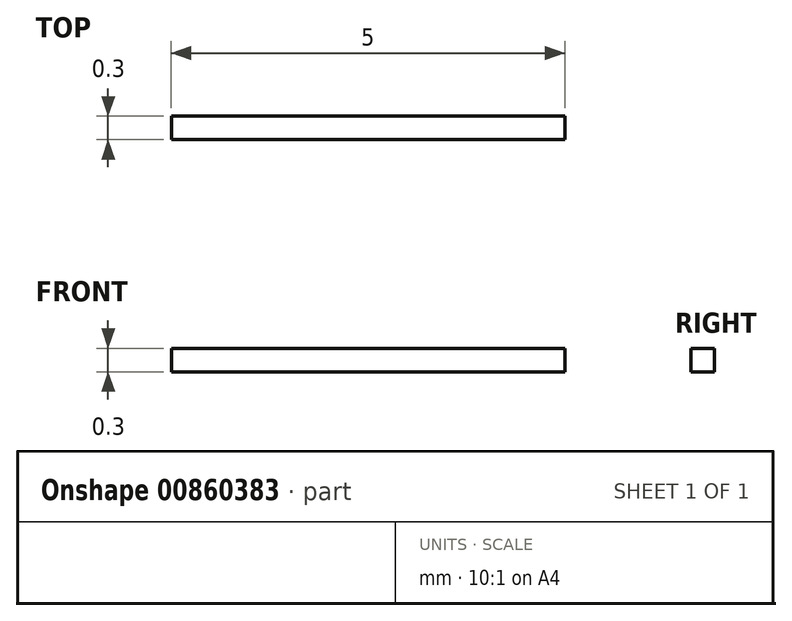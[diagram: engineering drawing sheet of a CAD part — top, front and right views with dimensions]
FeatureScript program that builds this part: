
annotation { "Feature Type Name" : "Feature", "Feature Type Description" : "" }
export const myFeature = defineFeature(function(context is Context, id is Id, definition is map)
    precondition{}
    {
        {
            var Q0;
            Q0=qCreatedBy(makeId("Top.planeOp"),FACE);
            var sketch = newSketch(context, id + "F0", { "sketchPlane" : qUnion([Q0])});
            skLineSegment(sketch, "E0.bottom", {"start": v(2.5, -0.15) * mm, "end": v(-2.5, -0.15) * mm});
            skLineSegment(sketch, "E0.top", {"start": v(2.5, 0.15) * mm, "end": v(-2.5, 0.15) * mm});
            skLineSegment(sketch, "E0.left", {"start": v(2.5, -0.15) * mm, "end": v(2.5, 0.15) * mm});
            skLineSegment(sketch, "E0.right", {"start": v(-2.5, -0.15) * mm, "end": v(-2.5, 0.15) * mm});
            skPoint(sketch, "E0.middle", {"position": v(0, 0) * mm});
            skSolve(sketch);
        }
        {
            var Q0;
            Q0=makeQuery(id+"F0.imprint","IMPRINT",FACE,{"disambiguationData":[TD([[makeQuery(id+"F0.imprint","IMPRINT",EDGE,{"derivedFrom":sQuery(id+"F0.wireOp",EDGE,"E0.bottom")}),-1.0]])]});
            extrude(context, id + "F1", {"entities" : qUnion([Q0]), "depth" : 0.3 * mm, "offsetDistance" : 25 * mm});
        }
    });
